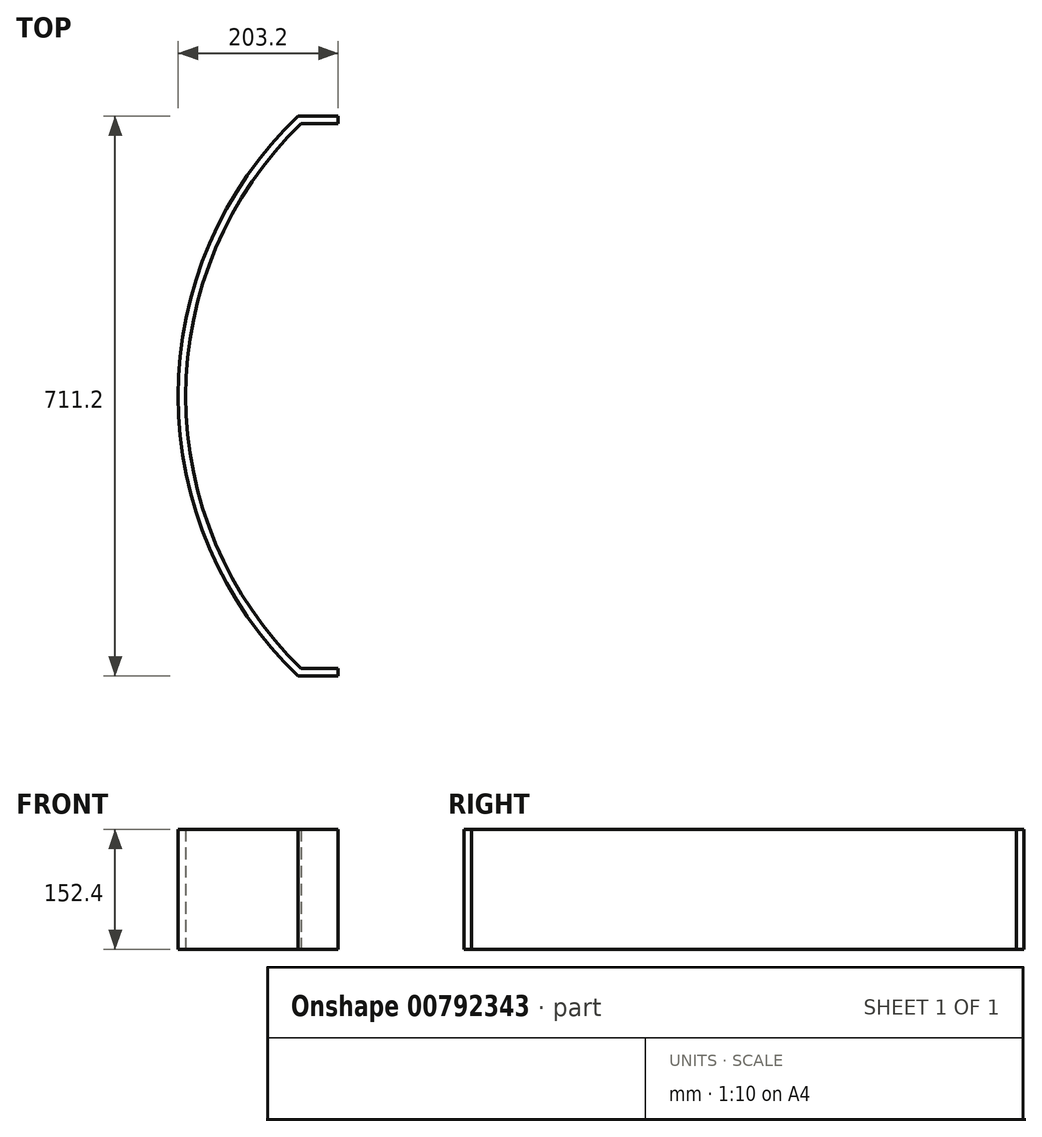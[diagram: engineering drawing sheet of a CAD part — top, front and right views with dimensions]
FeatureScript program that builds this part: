
annotation { "Feature Type Name" : "Feature", "Feature Type Description" : "" }
export const myFeature = defineFeature(function(context is Context, id is Id, definition is map)
    precondition{}
    {
        {
            var Q0;
            Q0=qCreatedBy(makeId("Top.planeOp"),FACE);
            var sketch = newSketch(context, id + "F0", { "sketchPlane" : qUnion([Q0])});
            skArc(sketch, "E0", {"start": v(0, 711.2) * mm, "mid": v(-152.4, 355.6) * mm, "end": v(0, 0) * mm});
            skLineSegment(sketch, "E1", {"start": v(0, 711.2) * mm, "end": v(50.8, 711.2) * mm});
            skLineSegment(sketch, "E2", {"start": v(0, 0) * mm, "end": v(50.8, 0) * mm});
            skLineSegment(sketch, "E3", {"start": v(-152.4, 355.6) * mm, "end": v(-152.4, 0) * mm, "construction": true});
            skLineSegment(sketch, "E4.0", {"start": v(3.83, 701.68) * mm, "end": v(50.8, 701.68) * mm});
            skArc(sketch, "E4.1", {"start": v(3.83, 701.67) * mm, "mid": v(-142.87, 355.6) * mm, "end": v(3.83, 9.53) * mm});
            skLineSegment(sketch, "E4.2", {"start": v(3.83, 9.53) * mm, "end": v(50.8, 9.53) * mm});
            skLineSegment(sketch, "E5", {"start": v(50.8, 701.68) * mm, "end": v(50.8, 711.2) * mm});
            skLineSegment(sketch, "E6", {"start": v(50.8, 9.53) * mm, "end": v(50.8, 0) * mm});
            skSolve(sketch);
        }
        {
            var Q0;
            Q0=makeQuery(id+"F0.imprint","IMPRINT",FACE,{"disambiguationData":[TD([[makeQuery(id+"F0.imprint","IMPRINT",EDGE,{"derivedFrom":sQuery(id+"F0.wireOp",EDGE,"E0")}),1.0]])]});
            extrude(context, id + "F1", {"entities" : qUnion([Q0]), "depth" : 152.4 * mm, "offsetDistance" : 25.4 * mm});
        }
    });
